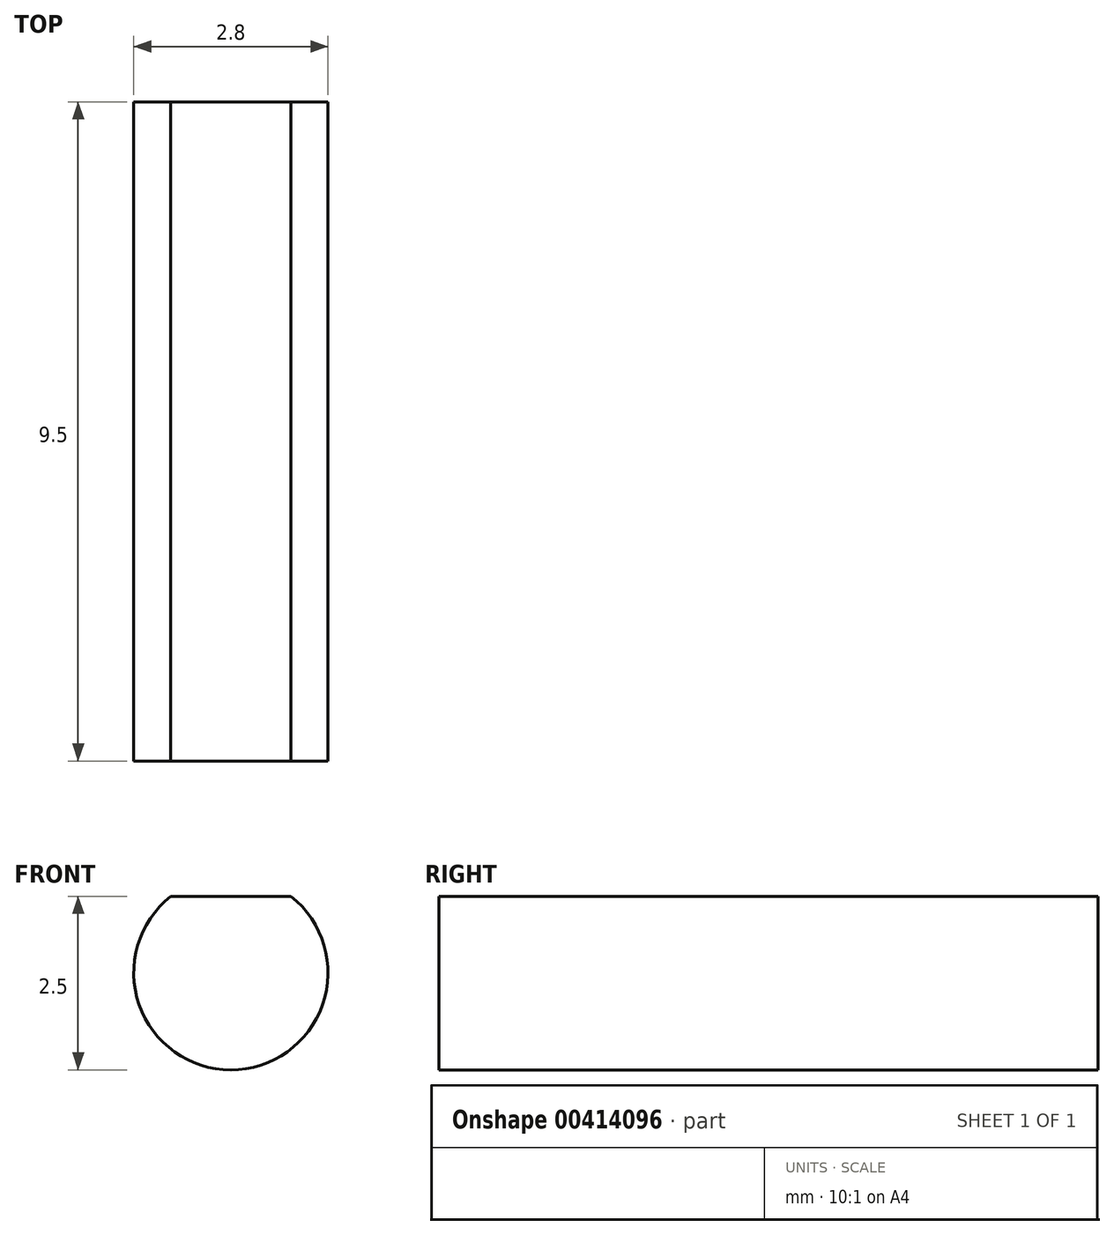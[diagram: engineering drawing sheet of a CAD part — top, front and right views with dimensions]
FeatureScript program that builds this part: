
annotation { "Feature Type Name" : "Feature", "Feature Type Description" : "" }
export const myFeature = defineFeature(function(context is Context, id is Id, definition is map)
    precondition{}
    {
        {
            var Q0;
            Q0=qCreatedBy(makeId("Front.planeOp"),FACE);
            var sketch = newSketch(context, id + "F0", { "sketchPlane" : qUnion([Q0])});
            skArc(sketch, "E0", {"start": v(-0.87, 1.1) * mm, "mid": v(0, -1.4) * mm, "end": v(0.87, 1.1) * mm});
            skLineSegment(sketch, "E1", {"start": v(0, 1.1) * mm, "end": v(0.87, 1.1) * mm});
            skLineSegment(sketch, "E2", {"start": v(0.87, 1.1) * mm, "end": v(-0.87, 1.1) * mm});
            skPoint(sketch, "E3.orphan", {"position": v(0, 1.4) * mm});
            skSolve(sketch);
        }
        {
            var Q0;
            {var subQ0=sQuery(id+"F0.wireOp",EDGE,"E0");Q0=makeQuery(id+"F0.imprint","IMPRINT",FACE,{"disambiguationData":[TD([[makeQuery(id+"F0.imprint","IMPRINT",EDGE,{"derivedFrom":subQ0}),1.0]])]});}
            extrude(context, id + "F1", {"entities" : qUnion([Q0]), "depth" : 9.5 * mm});
        }
    });
